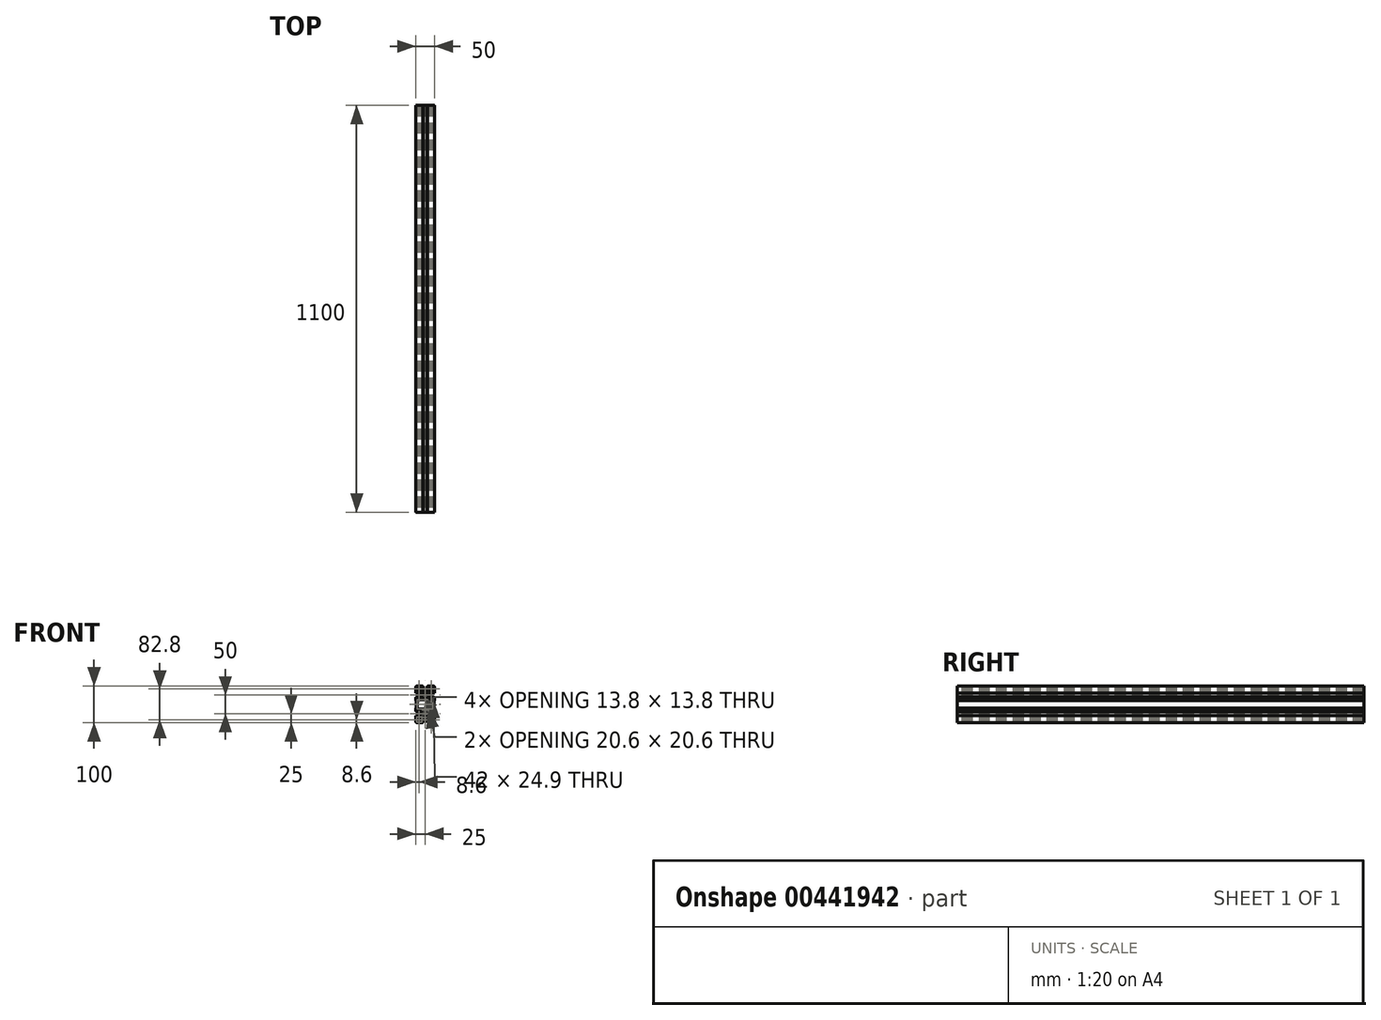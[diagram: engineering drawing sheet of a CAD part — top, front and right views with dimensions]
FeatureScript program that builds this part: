
annotation { "Feature Type Name" : "Feature", "Feature Type Description" : "" }
export const myFeature = defineFeature(function(context is Context, id is Id, definition is map)
    precondition{}
    {
        {
            var Q0;
            Q0=qCreatedBy(makeId("Front.planeOp"),FACE);
            var sketch = newSketch(context, id + "F0", { "sketchPlane" : qUnion([Q0])});
            skLineSegment(sketch, "E0", {"start": v(0, 0) * mm, "end": v(0, 25) * mm, "construction": true});
            skLineSegment(sketch, "E1", {"start": v(0, 0) * mm, "end": v(0, -25) * mm, "construction": true});
            skCircle(sketch, "E2", {"center": v(0, 25) * mm, "radius": 10 * mm});
            skCircle(sketch, "E3", {"center": v(0, -25) * mm, "radius": 10 * mm});
            skLineSegment(sketch, "E4.bottom", {"start": v(25, 50) * mm, "end": v(-25, 50) * mm});
            skLineSegment(sketch, "E4.top", {"start": v(25, -50) * mm, "end": v(-25, -50) * mm});
            skLineSegment(sketch, "E4.left", {"start": v(25, 50) * mm, "end": v(25, -50) * mm});
            skLineSegment(sketch, "E4.right", {"start": v(-25, 50) * mm, "end": v(-25, -50) * mm});
            skPoint(sketch, "E4.middle", {"position": v(0, 0) * mm});
            skSolve(sketch);
        }
        {
            var Q0;
            Q0=makeQuery(id+"F0.imprint","IMPRINT",FACE,{"disambiguationData":[TD([[makeQuery(id+"F0.imprint","IMPRINT",EDGE,{"derivedFrom":sQuery(id+"F0.wireOp",EDGE,"E2")}),-1.0]])]});
            cPlane(context, id + "F1", {"entities" : qUnion([Q0]), "cplaneType" : CPlaneType.OFFSET, "offset" : 25 * mm, "width" : 150 * mm, "height" : 150 * mm});
        }
        {
            var Q0;
            Q0=qCreatedBy(makeId("Front.planeOp"),FACE);
            var sketch = newSketch(context, id + "F2", { "sketchPlane" : qUnion([Q0])});
            skArc(sketch, "E5", {"start": v(-18.8, 37.67) * mm, "mid": v(-20.11, 37.42) * mm, "end": v(-20.7, 36.23) * mm});
            skArc(sketch, "E6", {"start": v(20.7, 36.23) * mm, "mid": v(20.11, 37.42) * mm, "end": v(18.8, 37.67) * mm});
            skArc(sketch, "E7", {"start": v(12.9, -40.52) * mm, "mid": v(12.51, -42.15) * mm, "end": v(12.67, -43.8) * mm});
            skArc(sketch, "E8", {"start": v(22, -50) * mm, "mid": v(24.12, -49.12) * mm, "end": v(25, -47) * mm});
            skArc(sketch, "E9", {"start": v(19, -47.27) * mm, "mid": v(21.04, -46.04) * mm, "end": v(22.27, -44) * mm});
            skArc(sketch, "E10", {"start": v(11.23, -45.7) * mm, "mid": v(12.42, -45.11) * mm, "end": v(12.67, -43.8) * mm});
            skArc(sketch, "E11", {"start": v(18.8, -37.67) * mm, "mid": v(20.11, -37.42) * mm, "end": v(20.7, -36.23) * mm});
            skArc(sketch, "E12", {"start": v(18.8, -37.67) * mm, "mid": v(17.14, -37.51) * mm, "end": v(15.52, -37.9) * mm});
            skArc(sketch, "E13", {"start": v(15.2, -37.85) * mm, "mid": v(15.35, -37.93) * mm, "end": v(15.52, -37.9) * mm});
            skArc(sketch, "E14", {"start": v(12.9, -40.52) * mm, "mid": v(12.93, -40.35) * mm, "end": v(12.84, -40.2) * mm});
            skArc(sketch, "E15", {"start": v(-4.53, -22.89) * mm, "mid": v(-5, -25) * mm, "end": v(-4.53, -27.11) * mm});
            skArc(sketch, "E16", {"start": v(4.53, -27.11) * mm, "mid": v(5, -25) * mm, "end": v(4.53, -22.89) * mm});
            skArc(sketch, "E17", {"start": v(-2.11, -29.53) * mm, "mid": v(0, -30) * mm, "end": v(2.11, -29.53) * mm});
            skArc(sketch, "E18", {"start": v(2.11, -20.47) * mm, "mid": v(0, -20) * mm, "end": v(-2.11, -20.47) * mm});
            skArc(sketch, "E19", {"start": v(-4.53, 27.11) * mm, "mid": v(-5, 25) * mm, "end": v(-4.53, 22.89) * mm});
            skArc(sketch, "E20", {"start": v(4.53, 22.89) * mm, "mid": v(5, 25) * mm, "end": v(4.53, 27.11) * mm});
            skArc(sketch, "E21", {"start": v(-2.11, 20.47) * mm, "mid": v(0, 20) * mm, "end": v(2.11, 20.47) * mm});
            skArc(sketch, "E22", {"start": v(15.52, 37.9) * mm, "mid": v(15.35, 37.93) * mm, "end": v(15.2, 37.84) * mm});
            skArc(sketch, "E23", {"start": v(15.52, 37.9) * mm, "mid": v(17.14, 37.51) * mm, "end": v(18.8, 37.67) * mm});
            skArc(sketch, "E24", {"start": v(2.11, 29.53) * mm, "mid": v(0, 30) * mm, "end": v(-2.11, 29.53) * mm});
            skArc(sketch, "E25", {"start": v(-12.67, -43.8) * mm, "mid": v(-12.51, -42.15) * mm, "end": v(-12.9, -40.52) * mm});
            skArc(sketch, "E26", {"start": v(-25, -47) * mm, "mid": v(-24.12, -49.12) * mm, "end": v(-22, -50) * mm});
            skArc(sketch, "E27", {"start": v(-12.67, -43.8) * mm, "mid": v(-12.42, -45.11) * mm, "end": v(-11.23, -45.7) * mm});
            skArc(sketch, "E28", {"start": v(-22.27, -44) * mm, "mid": v(-21.04, -46.04) * mm, "end": v(-19, -47.27) * mm});
            skArc(sketch, "E29", {"start": v(-20.7, -36.23) * mm, "mid": v(-20.11, -37.42) * mm, "end": v(-18.8, -37.67) * mm});
            skArc(sketch, "E30", {"start": v(-15.52, -37.9) * mm, "mid": v(-17.14, -37.51) * mm, "end": v(-18.8, -37.67) * mm});
            skArc(sketch, "E31", {"start": v(-12.84, -40.2) * mm, "mid": v(-12.93, -40.35) * mm, "end": v(-12.9, -40.52) * mm});
            skArc(sketch, "E32", {"start": v(-15.52, -37.9) * mm, "mid": v(-15.35, -37.93) * mm, "end": v(-15.2, -37.85) * mm});
            skArc(sketch, "E33", {"start": v(-18.8, 37.67) * mm, "mid": v(-17.14, 37.51) * mm, "end": v(-15.52, 37.9) * mm});
            skArc(sketch, "E34", {"start": v(-15.2, 37.84) * mm, "mid": v(-15.35, 37.93) * mm, "end": v(-15.52, 37.9) * mm});
            skArc(sketch, "E35", {"start": v(25, 47) * mm, "mid": v(24.12, 49.12) * mm, "end": v(22, 50) * mm});
            skArc(sketch, "E36", {"start": v(22.27, 44) * mm, "mid": v(21.04, 46.04) * mm, "end": v(19, 47.27) * mm});
            skArc(sketch, "E37", {"start": v(12.67, 43.8) * mm, "mid": v(12.42, 45.11) * mm, "end": v(11.23, 45.7) * mm});
            skArc(sketch, "E38", {"start": v(12.67, 43.8) * mm, "mid": v(12.51, 42.14) * mm, "end": v(12.9, 40.52) * mm});
            skArc(sketch, "E39", {"start": v(12.84, 40.2) * mm, "mid": v(12.93, 40.35) * mm, "end": v(12.9, 40.52) * mm});
            skArc(sketch, "E40", {"start": v(-22, 50) * mm, "mid": v(-24.12, 49.12) * mm, "end": v(-25, 47) * mm});
            skArc(sketch, "E41", {"start": v(-11.23, 45.7) * mm, "mid": v(-12.42, 45.11) * mm, "end": v(-12.67, 43.8) * mm});
            skArc(sketch, "E42", {"start": v(-12.9, 40.52) * mm, "mid": v(-12.93, 40.35) * mm, "end": v(-12.84, 40.2) * mm});
            skArc(sketch, "E43", {"start": v(-12.9, 40.52) * mm, "mid": v(-12.51, 42.14) * mm, "end": v(-12.67, 43.8) * mm});
            skArc(sketch, "E44", {"start": v(-19, 47.27) * mm, "mid": v(-21.04, 46.04) * mm, "end": v(-22.27, 44) * mm});
            skLineSegment(sketch, "E45", {"start": v(-9.54, 36.88) * mm, "end": v(-12.84, 40.2) * mm});
            skLineSegment(sketch, "E46", {"start": v(-25, 47) * mm, "end": v(-25, 30.8) * mm});
            skLineSegment(sketch, "E47", {"start": v(-23.3, 44) * mm, "end": v(-23.3, 34.5) * mm});
            skLineSegment(sketch, "E48", {"start": v(10.05, 39.8) * mm, "end": v(7.75, 37.5) * mm});
            skLineSegment(sketch, "E49", {"start": v(12.84, 40.2) * mm, "end": v(9.54, 36.88) * mm});
            skLineSegment(sketch, "E50", {"start": v(25, 30.8) * mm, "end": v(25, 47) * mm});
            skLineSegment(sketch, "E51", {"start": v(23.3, 34.5) * mm, "end": v(23.3, 44) * mm});
            skLineSegment(sketch, "E52", {"start": v(-7.75, 37.5) * mm, "end": v(-10.05, 39.8) * mm});
            skLineSegment(sketch, "E53", {"start": v(-2, 35.3) * mm, "end": v(-8.01, 35.3) * mm});
            skLineSegment(sketch, "E54", {"start": v(7.75, 37.5) * mm, "end": v(-7.75, 37.5) * mm});
            skLineSegment(sketch, "E55", {"start": v(-4.53, 22.89) * mm, "end": v(-7.7, 21.4) * mm});
            skLineSegment(sketch, "E56", {"start": v(-8.01, 14.7) * mm, "end": v(-2, 14.7) * mm});
            skLineSegment(sketch, "E57", {"start": v(-7.7, 28.6) * mm, "end": v(-4.53, 27.11) * mm});
            skLineSegment(sketch, "E58", {"start": v(-8.01, -35.3) * mm, "end": v(-2, -35.3) * mm});
            skLineSegment(sketch, "E59", {"start": v(-2, -14.7) * mm, "end": v(-8.01, -14.7) * mm});
            skLineSegment(sketch, "E60", {"start": v(-7.7, -21.4) * mm, "end": v(-4.53, -22.89) * mm});
            skLineSegment(sketch, "E61", {"start": v(-4.53, -27.11) * mm, "end": v(-7.7, -28.6) * mm});
            skLineSegment(sketch, "E62", {"start": v(-7.75, -37.5) * mm, "end": v(7.75, -37.5) * mm});
            skLineSegment(sketch, "E63", {"start": v(-5, -44) * mm, "end": v(-10.05, -44) * mm});
            skLineSegment(sketch, "E64", {"start": v(-22, -50) * mm, "end": v(-5.8, -50) * mm});
            skLineSegment(sketch, "E65", {"start": v(21, 12.45) * mm, "end": v(-21, 12.45) * mm});
            skLineSegment(sketch, "E66", {"start": v(-21, -12.45) * mm, "end": v(21, -12.45) * mm});
            skLineSegment(sketch, "E67", {"start": v(24, -10) * mm, "end": v(24, 10) * mm});
            skLineSegment(sketch, "E68", {"start": v(21, -12.45) * mm, "end": v(21, 12.45) * mm});
            skLineSegment(sketch, "E69", {"start": v(-3.6, -32.7) * mm, "end": v(-2.11, -29.53) * mm});
            skLineSegment(sketch, "E70", {"start": v(2.11, -29.53) * mm, "end": v(3.6, -32.7) * mm});
            skLineSegment(sketch, "E71", {"start": v(10.3, -33.01) * mm, "end": v(10.3, -27) * mm});
            skLineSegment(sketch, "E72", {"start": v(12.5, -32.75) * mm, "end": v(12.5, -17.25) * mm});
            skLineSegment(sketch, "E73", {"start": v(19, -30) * mm, "end": v(19, -35.05) * mm});
            skLineSegment(sketch, "E74", {"start": v(25, -47) * mm, "end": v(25, -30.8) * mm});
            skLineSegment(sketch, "E75", {"start": v(10.05, -39.8) * mm, "end": v(10.05, -44) * mm});
            skLineSegment(sketch, "E76", {"start": v(23.3, -44) * mm, "end": v(23.3, -34.5) * mm});
            skLineSegment(sketch, "E77", {"start": v(5.8, -50) * mm, "end": v(22, -50) * mm});
            skLineSegment(sketch, "E78", {"start": v(9.5, -48.3) * mm, "end": v(19, -48.3) * mm});
            skLineSegment(sketch, "E79", {"start": v(22.27, -44) * mm, "end": v(23.3, -44) * mm});
            skLineSegment(sketch, "E80", {"start": v(19, -48.3) * mm, "end": v(19, -47.27) * mm});
            skLineSegment(sketch, "E81", {"start": v(-5.8, -50) * mm, "end": v(-5.8, -48.5) * mm});
            skLineSegment(sketch, "E82", {"start": v(5.8, -48.5) * mm, "end": v(5.8, -50) * mm});
            skLineSegment(sketch, "E83", {"start": v(10.05, -44) * mm, "end": v(5, -44) * mm});
            skLineSegment(sketch, "E84", {"start": v(11.23, -45.7) * mm, "end": v(9.5, -45.7) * mm});
            skLineSegment(sketch, "E85", {"start": v(5, -48.5) * mm, "end": v(5.8, -48.5) * mm});
            skLineSegment(sketch, "E86", {"start": v(5, -44) * mm, "end": v(5, -48.5) * mm});
            skLineSegment(sketch, "E87", {"start": v(9.5, -45.7) * mm, "end": v(9.5, -48.3) * mm});
            skLineSegment(sketch, "E88", {"start": v(-5.8, -48.5) * mm, "end": v(-5, -48.5) * mm});
            skLineSegment(sketch, "E89", {"start": v(-5, -48.5) * mm, "end": v(-5, -44) * mm});
            skLineSegment(sketch, "E90", {"start": v(14.8, -35.05) * mm, "end": v(12.5, -32.75) * mm});
            skLineSegment(sketch, "E91", {"start": v(15.2, -37.85) * mm, "end": v(11.88, -34.54) * mm});
            skLineSegment(sketch, "E92", {"start": v(19, -35.05) * mm, "end": v(14.8, -35.05) * mm});
            skLineSegment(sketch, "E93", {"start": v(20.7, -34.5) * mm, "end": v(20.7, -36.23) * mm});
            skLineSegment(sketch, "E94", {"start": v(23.3, -34.5) * mm, "end": v(20.7, -34.5) * mm});
            skLineSegment(sketch, "E95", {"start": v(9.54, -36.89) * mm, "end": v(12.84, -40.2) * mm});
            skLineSegment(sketch, "E96", {"start": v(7.75, -37.5) * mm, "end": v(10.05, -39.8) * mm});
            skLineSegment(sketch, "E97", {"start": v(3.6, -32.7) * mm, "end": v(2, -33.45) * mm});
            skLineSegment(sketch, "E98", {"start": v(2, -35.3) * mm, "end": v(8.01, -35.3) * mm});
            skLineSegment(sketch, "E99", {"start": v(11.88, -34.54) * mm, "end": v(9.54, -36.89) * mm});
            skLineSegment(sketch, "E100", {"start": v(8.01, -35.3) * mm, "end": v(10.3, -33.01) * mm});
            skLineSegment(sketch, "E101", {"start": v(-2, -35.3) * mm, "end": v(-2, -33.45) * mm});
            skLineSegment(sketch, "E102", {"start": v(-2, -33.45) * mm, "end": v(-3.6, -32.7) * mm});
            skLineSegment(sketch, "E103", {"start": v(2, -33.45) * mm, "end": v(2, -35.3) * mm});
            skLineSegment(sketch, "E104", {"start": v(-2.11, -20.47) * mm, "end": v(-3.6, -17.3) * mm});
            skLineSegment(sketch, "E105", {"start": v(10.3, -23) * mm, "end": v(10.3, -16.99) * mm});
            skLineSegment(sketch, "E106", {"start": v(3.6, -17.3) * mm, "end": v(2.11, -20.47) * mm});
            skLineSegment(sketch, "E107", {"start": v(19, -14.95) * mm, "end": v(19, -20) * mm});
            skLineSegment(sketch, "E108", {"start": v(23.5, -20) * mm, "end": v(23.5, -19.2) * mm});
            skLineSegment(sketch, "E109", {"start": v(25, -30.8) * mm, "end": v(23.5, -30.8) * mm});
            skLineSegment(sketch, "E110", {"start": v(23.5, -30.8) * mm, "end": v(23.5, -30) * mm});
            skLineSegment(sketch, "E111", {"start": v(23.5, -30) * mm, "end": v(19, -30) * mm});
            skLineSegment(sketch, "E112", {"start": v(19, -20) * mm, "end": v(23.5, -20) * mm});
            skLineSegment(sketch, "E113", {"start": v(10.3, -27) * mm, "end": v(8.45, -27) * mm});
            skLineSegment(sketch, "E114", {"start": v(8.45, -27) * mm, "end": v(7.7, -28.6) * mm});
            skLineSegment(sketch, "E115", {"start": v(7.7, -28.6) * mm, "end": v(4.53, -27.11) * mm});
            skLineSegment(sketch, "E116", {"start": v(4.53, -22.89) * mm, "end": v(7.7, -21.4) * mm});
            skLineSegment(sketch, "E117", {"start": v(7.7, -21.4) * mm, "end": v(8.45, -23) * mm});
            skLineSegment(sketch, "E118", {"start": v(8.45, -23) * mm, "end": v(10.3, -23) * mm});
            skLineSegment(sketch, "E119", {"start": v(12.5, -17.25) * mm, "end": v(14.8, -14.95) * mm});
            skLineSegment(sketch, "E120", {"start": v(25, -19.2) * mm, "end": v(25, -10) * mm});
            skLineSegment(sketch, "E121", {"start": v(23.5, -19.2) * mm, "end": v(25, -19.2) * mm});
            skLineSegment(sketch, "E122", {"start": v(14.8, -14.95) * mm, "end": v(19, -14.95) * mm});
            skLineSegment(sketch, "E123", {"start": v(25, -10) * mm, "end": v(24, -10) * mm});
            skLineSegment(sketch, "E124", {"start": v(8.01, -14.7) * mm, "end": v(2, -14.7) * mm});
            skLineSegment(sketch, "E125", {"start": v(2, -16.55) * mm, "end": v(3.6, -17.3) * mm});
            skLineSegment(sketch, "E126", {"start": v(10.3, -16.99) * mm, "end": v(8.01, -14.7) * mm});
            skLineSegment(sketch, "E127", {"start": v(-3.6, -17.3) * mm, "end": v(-2, -16.55) * mm});
            skLineSegment(sketch, "E128", {"start": v(-2, -16.55) * mm, "end": v(-2, -14.7) * mm});
            skLineSegment(sketch, "E129", {"start": v(2, -14.7) * mm, "end": v(2, -16.55) * mm});
            skLineSegment(sketch, "E130", {"start": v(-2, 14.7) * mm, "end": v(-2, 16.55) * mm});
            skLineSegment(sketch, "E131", {"start": v(2, 16.55) * mm, "end": v(2, 14.7) * mm});
            skLineSegment(sketch, "E132", {"start": v(8.01, 14.7) * mm, "end": v(10.3, 16.99) * mm});
            skLineSegment(sketch, "E133", {"start": v(25, 10) * mm, "end": v(25, 19.2) * mm});
            skLineSegment(sketch, "E134", {"start": v(24, 10) * mm, "end": v(25, 10) * mm});
            skLineSegment(sketch, "E135", {"start": v(2, 14.7) * mm, "end": v(8.01, 14.7) * mm});
            skLineSegment(sketch, "E136", {"start": v(12.5, 17.25) * mm, "end": v(12.5, 32.75) * mm});
            skLineSegment(sketch, "E137", {"start": v(14.8, 14.95) * mm, "end": v(12.5, 17.25) * mm});
            skLineSegment(sketch, "E138", {"start": v(25, 19.2) * mm, "end": v(23.5, 19.2) * mm});
            skLineSegment(sketch, "E139", {"start": v(19, 14.95) * mm, "end": v(14.8, 14.95) * mm});
            skLineSegment(sketch, "E140", {"start": v(19, 20) * mm, "end": v(19, 14.95) * mm});
            skLineSegment(sketch, "E141", {"start": v(23.5, 19.2) * mm, "end": v(23.5, 20) * mm});
            skLineSegment(sketch, "E142", {"start": v(23.5, 20) * mm, "end": v(19, 20) * mm});
            skLineSegment(sketch, "E143", {"start": v(10.3, 16.99) * mm, "end": v(10.3, 23) * mm});
            skLineSegment(sketch, "E144", {"start": v(2.11, 20.47) * mm, "end": v(3.6, 17.3) * mm});
            skLineSegment(sketch, "E145", {"start": v(3.6, 17.3) * mm, "end": v(2, 16.55) * mm});
            skLineSegment(sketch, "E146", {"start": v(-2, 16.55) * mm, "end": v(-3.6, 17.3) * mm});
            skLineSegment(sketch, "E147", {"start": v(-3.6, 17.3) * mm, "end": v(-2.11, 20.47) * mm});
            skLineSegment(sketch, "E148", {"start": v(10.3, 23) * mm, "end": v(8.45, 23) * mm});
            skLineSegment(sketch, "E149", {"start": v(8.45, 23) * mm, "end": v(7.7, 21.4) * mm});
            skLineSegment(sketch, "E150", {"start": v(7.7, 21.4) * mm, "end": v(4.53, 22.89) * mm});
            skLineSegment(sketch, "E151", {"start": v(12.5, 32.75) * mm, "end": v(14.8, 35.05) * mm});
            skLineSegment(sketch, "E152", {"start": v(11.88, 34.54) * mm, "end": v(15.2, 37.84) * mm});
            skLineSegment(sketch, "E153", {"start": v(19, 35.05) * mm, "end": v(19, 30) * mm});
            skLineSegment(sketch, "E154", {"start": v(23.5, 30.8) * mm, "end": v(25, 30.8) * mm});
            skLineSegment(sketch, "E155", {"start": v(23.5, 30) * mm, "end": v(23.5, 30.8) * mm});
            skLineSegment(sketch, "E156", {"start": v(19, 30) * mm, "end": v(23.5, 30) * mm});
            skLineSegment(sketch, "E157", {"start": v(14.8, 35.05) * mm, "end": v(19, 35.05) * mm});
            skLineSegment(sketch, "E158", {"start": v(20.7, 34.5) * mm, "end": v(23.3, 34.5) * mm});
            skLineSegment(sketch, "E159", {"start": v(20.7, 36.23) * mm, "end": v(20.7, 34.5) * mm});
            skLineSegment(sketch, "E160", {"start": v(-2.11, 29.53) * mm, "end": v(-3.6, 32.7) * mm});
            skLineSegment(sketch, "E161", {"start": v(10.3, 27) * mm, "end": v(10.3, 33.01) * mm});
            skLineSegment(sketch, "E162", {"start": v(3.6, 32.7) * mm, "end": v(2.11, 29.53) * mm});
            skLineSegment(sketch, "E163", {"start": v(4.53, 27.11) * mm, "end": v(7.7, 28.6) * mm});
            skLineSegment(sketch, "E164", {"start": v(7.7, 28.6) * mm, "end": v(8.45, 27) * mm});
            skLineSegment(sketch, "E165", {"start": v(8.45, 27) * mm, "end": v(10.3, 27) * mm});
            skLineSegment(sketch, "E166", {"start": v(8.01, 35.3) * mm, "end": v(2, 35.3) * mm});
            skLineSegment(sketch, "E167", {"start": v(2, 33.45) * mm, "end": v(3.6, 32.7) * mm});
            skLineSegment(sketch, "E168", {"start": v(10.3, 33.01) * mm, "end": v(8.01, 35.3) * mm});
            skLineSegment(sketch, "E169", {"start": v(9.54, 36.88) * mm, "end": v(11.88, 34.54) * mm});
            skLineSegment(sketch, "E170", {"start": v(-3.6, 32.7) * mm, "end": v(-2, 33.45) * mm});
            skLineSegment(sketch, "E171", {"start": v(2, 35.3) * mm, "end": v(2, 33.45) * mm});
            skLineSegment(sketch, "E172", {"start": v(-2, 33.45) * mm, "end": v(-2, 35.3) * mm});
            skLineSegment(sketch, "E173", {"start": v(-24, 10) * mm, "end": v(-24, -10) * mm});
            skLineSegment(sketch, "E174", {"start": v(-21, 12.45) * mm, "end": v(-21, -12.45) * mm});
            skLineSegment(sketch, "E175", {"start": v(-19, -35.05) * mm, "end": v(-19, -30) * mm});
            skLineSegment(sketch, "E176", {"start": v(-12.5, -17.25) * mm, "end": v(-12.5, -32.75) * mm});
            skLineSegment(sketch, "E177", {"start": v(-10.3, -27) * mm, "end": v(-10.3, -33.01) * mm});
            skLineSegment(sketch, "E178", {"start": v(-25, -30.8) * mm, "end": v(-25, -47) * mm});
            skLineSegment(sketch, "E179", {"start": v(-23.3, -34.5) * mm, "end": v(-23.3, -44) * mm});
            skLineSegment(sketch, "E180", {"start": v(-10.05, -44) * mm, "end": v(-10.05, -39.8) * mm});
            skLineSegment(sketch, "E181", {"start": v(-19, -48.3) * mm, "end": v(-9.5, -48.3) * mm});
            skLineSegment(sketch, "E182", {"start": v(-9.5, -45.7) * mm, "end": v(-11.23, -45.7) * mm});
            skLineSegment(sketch, "E183", {"start": v(-9.5, -48.3) * mm, "end": v(-9.5, -45.7) * mm});
            skLineSegment(sketch, "E184", {"start": v(-23.3, -44) * mm, "end": v(-22.27, -44) * mm});
            skLineSegment(sketch, "E185", {"start": v(-19, -47.27) * mm, "end": v(-19, -48.3) * mm});
            skLineSegment(sketch, "E186", {"start": v(-12.84, -40.2) * mm, "end": v(-9.54, -36.89) * mm});
            skLineSegment(sketch, "E187", {"start": v(-11.88, -34.54) * mm, "end": v(-15.2, -37.85) * mm});
            skLineSegment(sketch, "E188", {"start": v(-10.05, -39.8) * mm, "end": v(-7.75, -37.5) * mm});
            skLineSegment(sketch, "E189", {"start": v(-14.8, -35.05) * mm, "end": v(-19, -35.05) * mm});
            skLineSegment(sketch, "E190", {"start": v(-12.5, -32.75) * mm, "end": v(-14.8, -35.05) * mm});
            skLineSegment(sketch, "E191", {"start": v(-9.54, -36.89) * mm, "end": v(-11.88, -34.54) * mm});
            skLineSegment(sketch, "E192", {"start": v(-10.3, -33.01) * mm, "end": v(-8.01, -35.3) * mm});
            skLineSegment(sketch, "E193", {"start": v(-20.7, -36.23) * mm, "end": v(-20.7, -34.5) * mm});
            skLineSegment(sketch, "E194", {"start": v(-20.7, -34.5) * mm, "end": v(-23.3, -34.5) * mm});
            skLineSegment(sketch, "E195", {"start": v(-23.5, -19.2) * mm, "end": v(-23.5, -20) * mm});
            skLineSegment(sketch, "E196", {"start": v(-19, -20) * mm, "end": v(-19, -14.95) * mm});
            skLineSegment(sketch, "E197", {"start": v(-10.3, -16.99) * mm, "end": v(-10.3, -23) * mm});
            skLineSegment(sketch, "E198", {"start": v(-7.7, -28.6) * mm, "end": v(-8.45, -27) * mm});
            skLineSegment(sketch, "E199", {"start": v(-8.45, -27) * mm, "end": v(-10.3, -27) * mm});
            skLineSegment(sketch, "E200", {"start": v(-23.5, -30.8) * mm, "end": v(-25, -30.8) * mm});
            skLineSegment(sketch, "E201", {"start": v(-23.5, -30) * mm, "end": v(-23.5, -30.8) * mm});
            skLineSegment(sketch, "E202", {"start": v(-19, -30) * mm, "end": v(-23.5, -30) * mm});
            skLineSegment(sketch, "E203", {"start": v(-8.45, -23) * mm, "end": v(-7.7, -21.4) * mm});
            skLineSegment(sketch, "E204", {"start": v(-10.3, -23) * mm, "end": v(-8.45, -23) * mm});
            skLineSegment(sketch, "E205", {"start": v(-23.5, -20) * mm, "end": v(-19, -20) * mm});
            skLineSegment(sketch, "E206", {"start": v(-25, -10) * mm, "end": v(-25, -19.2) * mm});
            skLineSegment(sketch, "E207", {"start": v(-19, -14.95) * mm, "end": v(-14.8, -14.95) * mm});
            skLineSegment(sketch, "E208", {"start": v(-14.8, -14.95) * mm, "end": v(-12.5, -17.25) * mm});
            skLineSegment(sketch, "E209", {"start": v(-8.01, -14.7) * mm, "end": v(-10.3, -16.99) * mm});
            skLineSegment(sketch, "E210", {"start": v(-25, -19.2) * mm, "end": v(-23.5, -19.2) * mm});
            skLineSegment(sketch, "E211", {"start": v(-24, -10) * mm, "end": v(-25, -10) * mm});
            skLineSegment(sketch, "E212", {"start": v(-25, 19.2) * mm, "end": v(-25, 10) * mm});
            skLineSegment(sketch, "E213", {"start": v(-10.3, 16.99) * mm, "end": v(-8.01, 14.7) * mm});
            skLineSegment(sketch, "E214", {"start": v(-25, 10) * mm, "end": v(-24, 10) * mm});
            skLineSegment(sketch, "E215", {"start": v(-12.5, 32.75) * mm, "end": v(-12.5, 17.25) * mm});
            skLineSegment(sketch, "E216", {"start": v(-10.3, 23) * mm, "end": v(-10.3, 16.99) * mm});
            skLineSegment(sketch, "E217", {"start": v(-14.8, 14.95) * mm, "end": v(-19, 14.95) * mm});
            skLineSegment(sketch, "E218", {"start": v(-12.5, 17.25) * mm, "end": v(-14.8, 14.95) * mm});
            skLineSegment(sketch, "E219", {"start": v(-23.5, 19.2) * mm, "end": v(-25, 19.2) * mm});
            skLineSegment(sketch, "E220", {"start": v(-23.5, 20) * mm, "end": v(-23.5, 19.2) * mm});
            skLineSegment(sketch, "E221", {"start": v(-19, 14.95) * mm, "end": v(-19, 20) * mm});
            skLineSegment(sketch, "E222", {"start": v(-19, 20) * mm, "end": v(-23.5, 20) * mm});
            skLineSegment(sketch, "E223", {"start": v(-7.7, 21.4) * mm, "end": v(-8.45, 23) * mm});
            skLineSegment(sketch, "E224", {"start": v(-8.45, 23) * mm, "end": v(-10.3, 23) * mm});
            skLineSegment(sketch, "E225", {"start": v(-10.3, 33.01) * mm, "end": v(-10.3, 27) * mm});
            skLineSegment(sketch, "E226", {"start": v(-19, 30) * mm, "end": v(-19, 35.05) * mm});
            skLineSegment(sketch, "E227", {"start": v(-8.45, 27) * mm, "end": v(-7.7, 28.6) * mm});
            skLineSegment(sketch, "E228", {"start": v(-10.3, 27) * mm, "end": v(-8.45, 27) * mm});
            skLineSegment(sketch, "E229", {"start": v(-23.5, 30.8) * mm, "end": v(-23.5, 30) * mm});
            skLineSegment(sketch, "E230", {"start": v(-25, 30.8) * mm, "end": v(-23.5, 30.8) * mm});
            skLineSegment(sketch, "E231", {"start": v(-23.5, 30) * mm, "end": v(-19, 30) * mm});
            skLineSegment(sketch, "E232", {"start": v(-19, 35.05) * mm, "end": v(-14.8, 35.05) * mm});
            skLineSegment(sketch, "E233", {"start": v(-14.8, 35.05) * mm, "end": v(-12.5, 32.75) * mm});
            skLineSegment(sketch, "E234", {"start": v(-15.2, 37.84) * mm, "end": v(-11.88, 34.54) * mm});
            skLineSegment(sketch, "E235", {"start": v(-11.88, 34.54) * mm, "end": v(-9.54, 36.88) * mm});
            skLineSegment(sketch, "E236", {"start": v(-8.01, 35.3) * mm, "end": v(-10.3, 33.01) * mm});
            skLineSegment(sketch, "E237", {"start": v(-23.3, 34.5) * mm, "end": v(-20.7, 34.5) * mm});
            skLineSegment(sketch, "E238", {"start": v(-20.7, 34.5) * mm, "end": v(-20.7, 36.23) * mm});
            skLineSegment(sketch, "E239", {"start": v(-5.8, 50) * mm, "end": v(-22, 50) * mm});
            skLineSegment(sketch, "E240", {"start": v(-10.05, 44) * mm, "end": v(-5, 44) * mm});
            skLineSegment(sketch, "E241", {"start": v(-5.8, 48.5) * mm, "end": v(-5.8, 50) * mm});
            skLineSegment(sketch, "E242", {"start": v(5.8, 50) * mm, "end": v(5.8, 48.5) * mm});
            skLineSegment(sketch, "E243", {"start": v(19, 48.3) * mm, "end": v(9.5, 48.3) * mm});
            skLineSegment(sketch, "E244", {"start": v(19, 47.27) * mm, "end": v(19, 48.3) * mm});
            skLineSegment(sketch, "E245", {"start": v(23.3, 44) * mm, "end": v(22.27, 44) * mm});
            skLineSegment(sketch, "E246", {"start": v(10.05, 44) * mm, "end": v(10.05, 39.8) * mm});
            skLineSegment(sketch, "E247", {"start": v(5, 44) * mm, "end": v(10.05, 44) * mm});
            skLineSegment(sketch, "E248", {"start": v(5, 48.5) * mm, "end": v(5, 44) * mm});
            skLineSegment(sketch, "E249", {"start": v(5.8, 48.5) * mm, "end": v(5, 48.5) * mm});
            skLineSegment(sketch, "E250", {"start": v(9.5, 48.3) * mm, "end": v(9.5, 45.7) * mm});
            skLineSegment(sketch, "E251", {"start": v(9.5, 45.7) * mm, "end": v(11.23, 45.7) * mm});
            skLineSegment(sketch, "E252", {"start": v(-5, 48.5) * mm, "end": v(-5.8, 48.5) * mm});
            skLineSegment(sketch, "E253", {"start": v(-5, 44) * mm, "end": v(-5, 48.5) * mm});
            skLineSegment(sketch, "E254", {"start": v(22, 50) * mm, "end": v(5.8, 50) * mm});
            skLineSegment(sketch, "E255", {"start": v(-10.05, 39.8) * mm, "end": v(-10.05, 44) * mm});
            skLineSegment(sketch, "E256", {"start": v(-9.5, 48.3) * mm, "end": v(-19, 48.3) * mm});
            skLineSegment(sketch, "E257", {"start": v(-11.23, 45.7) * mm, "end": v(-9.5, 45.7) * mm});
            skLineSegment(sketch, "E258", {"start": v(-9.5, 45.7) * mm, "end": v(-9.5, 48.3) * mm});
            skLineSegment(sketch, "E259", {"start": v(-22.27, 44) * mm, "end": v(-23.3, 44) * mm});
            skLineSegment(sketch, "E260", {"start": v(-19, 48.3) * mm, "end": v(-19, 47.27) * mm});
            skLineSegment(sketch, "E261", {"start": v(31.28, 0) * mm, "end": v(-51.84, 0) * mm});
            skLineSegment(sketch, "E262", {"start": v(0, 67.76) * mm, "end": v(0, -64.44) * mm});
            skSolve(sketch);
        }
        {
            var Q0;
            Q0=makeQuery(id+"F2.imprint","IMPRINT",FACE,{"disambiguationData":[TD([[makeQuery(id+"F2.imprint","IMPRINT",EDGE,{"derivedFrom":sQuery(id+"F2.wireOp",EDGE,"E6")}),1.0]])]});
            var Q1;
            Q1=makeQuery(id+"F2.imprint","IMPRINT",FACE,{"disambiguationData":[TD([[makeQuery(id+"F2.imprint","IMPRINT",EDGE,{"derivedFrom":sQuery(id+"F2.wireOp",EDGE,"E5")}),1.0]])]});
            var Q2;
            Q2=makeQuery(id+"F2.imprint","IMPRINT",FACE,{"disambiguationData":[TD([[makeQuery(id+"F2.imprint","IMPRINT",EDGE,{"derivedFrom":sQuery(id+"F2.wireOp",EDGE,"E7")}),-1.0]])]});
            var Q3;
            Q3=makeQuery(id+"F2.imprint","IMPRINT",FACE,{"disambiguationData":[TD([[makeQuery(id+"F2.imprint","IMPRINT",EDGE,{"derivedFrom":sQuery(id+"F2.wireOp",EDGE,"E15")}),-1.0]])]});
            extrude(context, id + "F3", {"entities" : qUnion([Q0, Q1, Q2, Q3]), "oppositeDirection" : true, "depth" : 1100 * mm});
        }
    });
